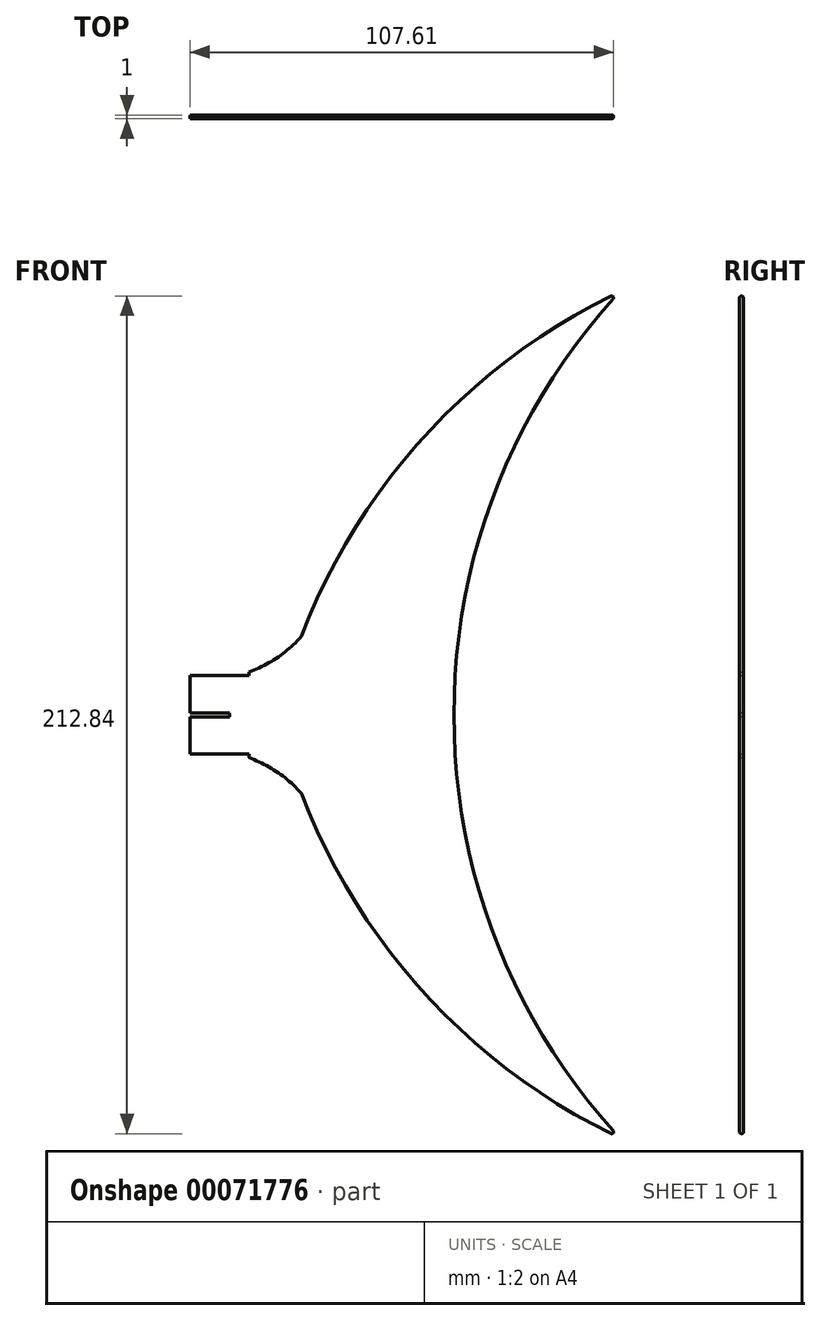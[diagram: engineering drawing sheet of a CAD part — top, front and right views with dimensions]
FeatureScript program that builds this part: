
annotation { "Feature Type Name" : "Feature", "Feature Type Description" : "" }
export const myFeature = defineFeature(function(context is Context, id is Id, definition is map)
    precondition{}
    {
        {
            var Q0;
            Q0=qCreatedBy(makeId("Front.planeOp"),FACE);
            var sketch = newSketch(context, id + "F0", { "sketchPlane" : qUnion([Q0])});
            skArc(sketch, "E0", {"start": v(0, 10.9) * mm, "mid": v(7.2, 14.55) * mm, "end": v(13.26, 19.9) * mm});
            skArc(sketch, "E1", {"start": v(94.25, 107.51) * mm, "mid": v(45.28, 71.53) * mm, "end": v(13.26, 19.9) * mm});
            skArc(sketch, "E2", {"start": v(94.25, 107.51) * mm, "mid": v(62.9, 57.79) * mm, "end": v(52.1, 0) * mm});
            skLineSegment(sketch, "E3", {"start": v(0, 10.9) * mm, "end": v(0, 0) * mm});
            skLineSegment(sketch, "E4", {"start": v(0, 0) * mm, "end": v(52.1, 0) * mm});
            skLineSegment(sketch, "E5.left", {"start": v(0, 0) * mm, "end": v(0, 0) * mm});
            skLineSegment(sketch, "E6.bottom", {"start": v(0, 0) * mm, "end": v(-15, 0) * mm});
            skLineSegment(sketch, "E6.top", {"start": v(0, 10) * mm, "end": v(-15, 10) * mm});
            skLineSegment(sketch, "E6.left", {"start": v(0, 0) * mm, "end": v(0, 10) * mm});
            skLineSegment(sketch, "E6.right", {"start": v(-15, 0) * mm, "end": v(-15, 10) * mm});
            skSolve(sketch);
        }
        {
            var Q0;
            Q0=makeQuery(id+"F0.imprint","IMPRINT",FACE,{"disambiguationData":[TD([[makeQuery(id+"F0.imprint","IMPRINT",EDGE,{"derivedFrom":sQuery(id+"F0.wireOp",EDGE,"E0")}),-1.0]])]});
            extrude(context, id + "F1", {"entities" : qUnion([Q0]), "endBound" : BoundingType.SYMMETRIC, "depth" : 1 * mm});
        }
        {
            var Q0;
            Q0=makeQuery(id+"F1.opExtrude","CAP_EDGE",EDGE,{"disambiguationData":[OSD([sQuery(id+"F0.wireOp",EDGE,"E0")])],"isStart":false});
            var Q1;
            Q1=makeQuery(id+"F1.opExtrude","CAP_EDGE",EDGE,{"disambiguationData":[OSD([sQuery(id+"F0.wireOp",EDGE,"E0")])],"isStart":true});
            var Q2;
            Q2=makeQuery(id+"F1.opExtrude","CAP_EDGE",EDGE,{"disambiguationData":[OSD([sQuery(id+"F0.wireOp",EDGE,"E1")])],"isStart":false});
            var Q3;
            Q3=makeQuery(id+"F1.opExtrude","CAP_EDGE",EDGE,{"disambiguationData":[OSD([sQuery(id+"F0.wireOp",EDGE,"E1")])],"isStart":true});
            var Q4;
            Q4=makeQuery(id+"F1.opExtrude","SWEPT_EDGE",EDGE,{"disambiguationData":[OSD([sQuery(id+"F0.wireOp",EDGE,"E0"),sQuery(id+"F0.wireOp",EDGE,"E1")])]});
            var Q5;
            Q5=makeQuery(id+"F1.opExtrude","SWEPT_EDGE",EDGE,{"disambiguationData":[OSD([sQuery(id+"F0.wireOp",EDGE,"E1"),sQuery(id+"F0.wireOp",EDGE,"E2")])]});
            var Q6;
            Q6=makeQuery(id+"F1.opExtrude","CAP_EDGE",EDGE,{"disambiguationData":[OSD([sQuery(id+"F0.wireOp",EDGE,"E2")])],"isStart":true});
            var Q7;
            Q7=makeQuery(id+"F1.opExtrude","CAP_EDGE",EDGE,{"disambiguationData":[OSD([sQuery(id+"F0.wireOp",EDGE,"E2")])],"isStart":false});
            fillet(context, id + "F2", {"entities" : qUnion([Q0, Q1, Q2, Q3, Q4, Q5, Q6, Q7]), "radius" : 0.5 * mm, "tangentPropagation" : true, "allowEdgeOverflow" : false});
        }
        {
            var Q0;
            Q0=makeQuery(id+"F1.opExtrude","SWEPT_BODY",BODY,{"disambiguationData":[OSD([sQuery(id+"F0.wireOp",EDGE,"E0"),sQuery(id+"F0.wireOp",EDGE,"E1"),sQuery(id+"F0.wireOp",EDGE,"E2"),sQuery(id+"F0.wireOp",EDGE,"E3"),sQuery(id+"F0.wireOp",EDGE,"E4")])]});
            var Q1;
            Q1=qCreatedBy(makeId("Top.planeOp"),FACE);
            mirror(context, id + "F3", {"operationType" : NewBodyOperationType.ADD, "entities" : qUnion([Q0]), "mirrorPlane" : qUnion([Q1])});
        }
        {
            var Q0;
            {var subQ3=sQuery(id+"F0.wireOp",EDGE,"E6.bottom");Q0=makeQuery(id+"F0.imprint","IMPRINT",FACE,{"disambiguationData":[TD([[makeQuery(id+"F0.imprint","IMPRINT",EDGE,{"derivedFrom":subQ3}),-1.0]])]});}
            extrude(context, id + "F4", {"entities" : qUnion([Q0]), "endBound" : BoundingType.SYMMETRIC, "depth" : 1 * mm});
        }
        {
            var Q0;
            Q0=makeQuery(id+"F4.opExtrude","SWEPT_BODY",BODY,{"disambiguationData":[OSD([sQuery(id+"F0.wireOp",EDGE,"E6.bottom"),sQuery(id+"F0.wireOp",EDGE,"E6.top"),sQuery(id+"F0.wireOp",EDGE,"E6.left"),sQuery(id+"F0.wireOp",EDGE,"E6.right")])]});
            var Q1;
            Q1=qCreatedBy(makeId("Top.planeOp"),FACE);
            mirror(context, id + "F5", {"operationType" : NewBodyOperationType.ADD, "entities" : qUnion([Q0]), "mirrorPlane" : qUnion([Q1])});
        }
        {
            var Q0;
            {var subQ0=makeQuery(id+"F4.opExtrude","CAP_FACE",FACE,{"disambiguationData":[OSD([sQuery(id+"F0.wireOp",EDGE,"E6.bottom"),sQuery(id+"F0.wireOp",EDGE,"E6.top"),sQuery(id+"F0.wireOp",EDGE,"E6.left"),sQuery(id+"F0.wireOp",EDGE,"E6.right")])],"isStart":false});Q0=makeQuery(id+"F5.boolean.opBoolean","MERGE",FACE,{"derivedFrom":[subQ0,makeQuery(id+"F5.opPattern","COPY",FACE,{"derivedFrom":subQ0,"instanceName":"1"})]});}
            var sketch = newSketch(context, id + "F6", { "sketchPlane" : qUnion([Q0])});
            skLineSegment(sketch, "E7.bottom", {"start": v(-5, -0.5) * mm, "end": v(-25, -0.5) * mm});
            skLineSegment(sketch, "E7.top", {"start": v(-5, 0.5) * mm, "end": v(-25, 0.5) * mm});
            skLineSegment(sketch, "E7.left", {"start": v(-5, -0.5) * mm, "end": v(-5, 0.5) * mm});
            skLineSegment(sketch, "E7.right", {"start": v(-25, -0.5) * mm, "end": v(-25, 0.5) * mm});
            skPoint(sketch, "E7.middle", {"position": v(-15, 0) * mm});
            skSolve(sketch);
        }
        {
            var Q0;
            {var subQ0=sQuery(id+"F6.wireOp",EDGE,"E7.left");Q0=makeQuery(id+"F6.imprint","IMPRINT",FACE,{"disambiguationData":[TD([[makeQuery(id+"F6.imprint","IMPRINT",EDGE,{"derivedFrom":subQ0}),1.0]])]});}
            extrude(context, id + "F7", {"entities" : qUnion([Q0]), "operationType" : NewBodyOperationType.REMOVE, "endBound" : BoundingType.THROUGH_ALL, "oppositeDirection" : true, "depth" : 25 * mm});
        }
    });
